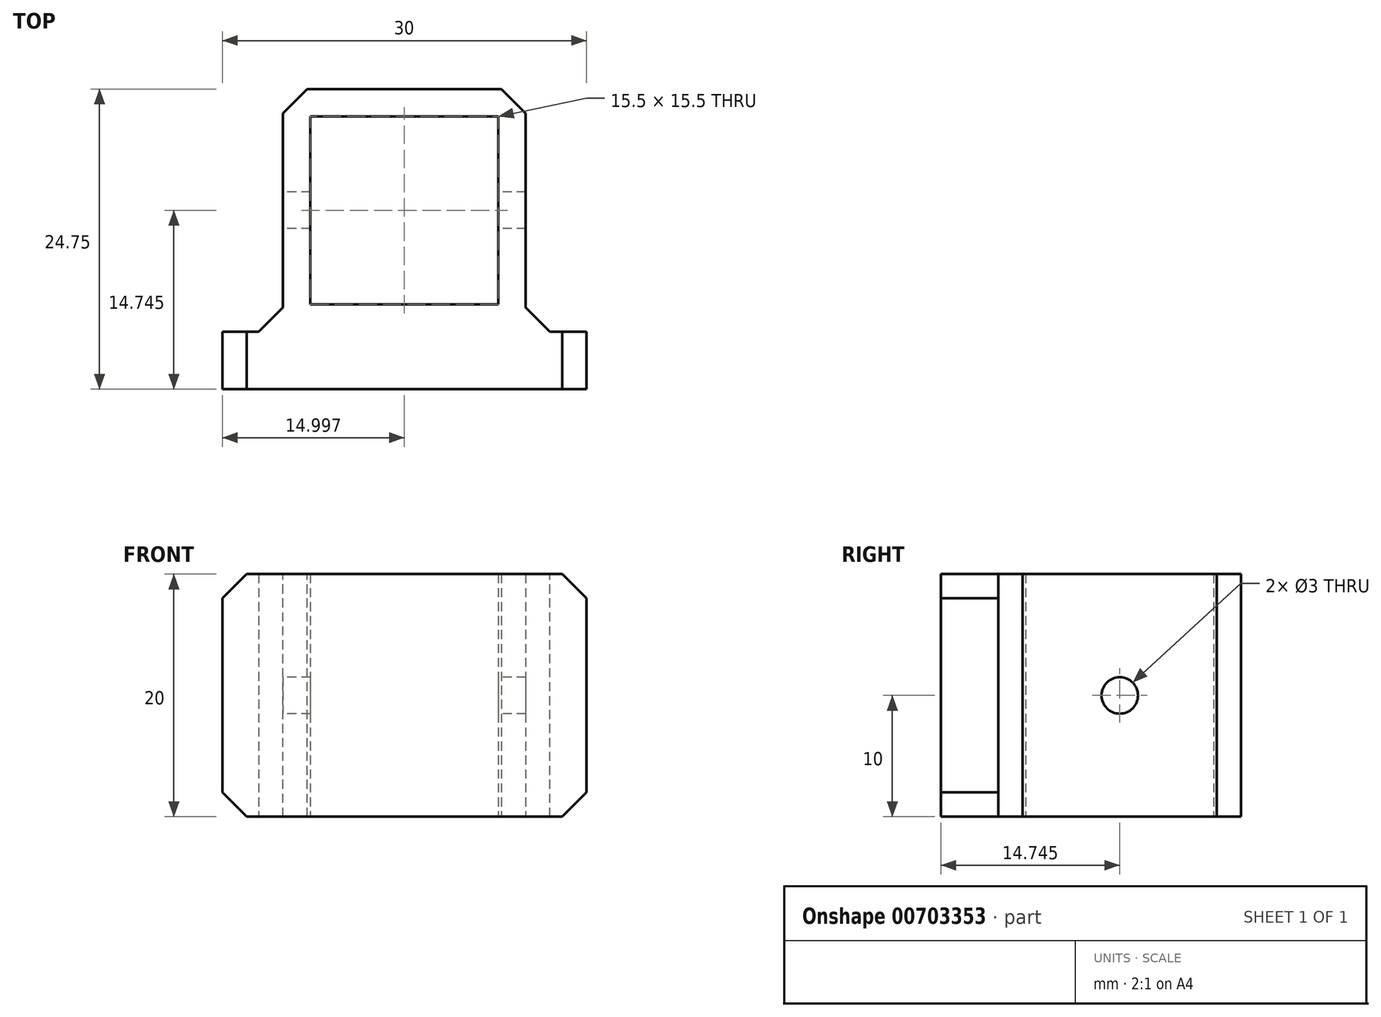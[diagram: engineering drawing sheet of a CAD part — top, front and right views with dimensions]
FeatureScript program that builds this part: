
annotation { "Feature Type Name" : "Feature", "Feature Type Description" : "" }
export const myFeature = defineFeature(function(context is Context, id is Id, definition is map)
    precondition{}
    {
        {
            var Q0;
            Q0=qCreatedBy(makeId("Top.planeOp"),FACE);
            var sketch = newSketch(context, id + "F0", { "sketchPlane" : qUnion([Q0])});
            skLineSegment(sketch, "E0.bottom", {"start": v(-33.17, 14.56) * mm, "end": v(-48.67, 14.56) * mm});
            skLineSegment(sketch, "E0.top", {"start": v(-33.17, 30.06) * mm, "end": v(-48.67, 30.06) * mm});
            skLineSegment(sketch, "E0.left", {"start": v(-33.17, 14.56) * mm, "end": v(-33.17, 30.06) * mm});
            skLineSegment(sketch, "E0.right", {"start": v(-48.67, 14.56) * mm, "end": v(-48.67, 30.06) * mm});
            skPoint(sketch, "E0.middle", {"position": v(-40.92, 22.3) * mm});
            skLineSegment(sketch, "E1.bottom", {"start": v(-50.92, 12.3) * mm, "end": v(-30.92, 12.3) * mm});
            skLineSegment(sketch, "E1.top", {"start": v(-50.92, 32.3) * mm, "end": v(-30.92, 32.3) * mm});
            skLineSegment(sketch, "E1.left", {"start": v(-50.92, 12.3) * mm, "end": v(-50.92, 32.3) * mm});
            skLineSegment(sketch, "E1.right", {"start": v(-30.92, 12.3) * mm, "end": v(-30.92, 32.3) * mm});
            skLineSegment(sketch, "E2", {"start": v(-50.92, 12.3) * mm, "end": v(-55.92, 12.3) * mm});
            skLineSegment(sketch, "E3", {"start": v(-55.92, 12.3) * mm, "end": v(-55.92, 7.56) * mm});
            skLineSegment(sketch, "E4", {"start": v(-55.92, 7.56) * mm, "end": v(-25.92, 7.56) * mm});
            skLineSegment(sketch, "E5", {"start": v(-30.92, 12.3) * mm, "end": v(-25.92, 12.3) * mm});
            skLineSegment(sketch, "E6", {"start": v(-25.92, 12.3) * mm, "end": v(-25.92, 7.56) * mm});
            skLineSegment(sketch, "E7", {"start": v(-13.17, 18.53) * mm, "end": v(-13.17, -6.15) * mm, "construction": true});
            skSolve(sketch);
        }
        {
            var Q0;
            Q0=makeQuery(id+"F0.imprint","IMPRINT",FACE,{"disambiguationData":[TD([[makeQuery(id+"F0.imprint","IMPRINT",EDGE,{"derivedFrom":sQuery(id+"F0.wireOp",EDGE,"E0.bottom")}),1.0]])]});
            var Q1;
            Q1=makeQuery(id+"F0.imprint","IMPRINT",FACE,{"disambiguationData":[TD([[makeQuery(id+"F0.imprint","IMPRINT",EDGE,{"derivedFrom":sQuery(id+"F0.wireOp",EDGE,"E1.bottom")}),-1.0]])]});
            extrude(context, id + "F1", {"entities" : qUnion([Q0, Q1]), "depth" : 20 * mm, "offsetDistance" : 25 * mm});
        }
        {
            var Q0;
            Q0=makeQuery(id+"F1.opExtrude","SWEPT_EDGE",EDGE,{"disambiguationData":[OSD([sQuery(id+"F0.wireOp",EDGE,"E1.top"),sQuery(id+"F0.wireOp",EDGE,"E1.left")])]});
            var Q1;
            Q1=makeQuery(id+"F1.opExtrude","SWEPT_EDGE",EDGE,{"disambiguationData":[OSD([sQuery(id+"F0.wireOp",EDGE,"E1.top"),sQuery(id+"F0.wireOp",EDGE,"E1.right")])]});
            var Q2;
            Q2=makeQuery(id+"F1.opExtrude","CAP_EDGE",EDGE,{"disambiguationData":[OSD([sQuery(id+"F0.wireOp",EDGE,"E6")])],"isStart":false});
            var Q3;
            Q3=makeQuery(id+"F1.opExtrude","CAP_EDGE",EDGE,{"disambiguationData":[OSD([sQuery(id+"F0.wireOp",EDGE,"E3")])],"isStart":false});
            var Q4;
            Q4=makeQuery(id+"F1.opExtrude","CAP_EDGE",EDGE,{"disambiguationData":[OSD([sQuery(id+"F0.wireOp",EDGE,"E3")])],"isStart":true});
            var Q5;
            Q5=makeQuery(id+"F1.opExtrude","CAP_EDGE",EDGE,{"disambiguationData":[OSD([sQuery(id+"F0.wireOp",EDGE,"E6")])],"isStart":true});
            var Q6;
            Q6=makeQuery(id+"F1.opExtrude","SWEPT_EDGE",EDGE,{"disambiguationData":[OSD([sQuery(id+"F0.wireOp",EDGE,"E1.bottom"),sQuery(id+"F0.wireOp",EDGE,"E1.right"),sQuery(id+"F0.wireOp",EDGE,"E5")])]});
            var Q7;
            Q7=makeQuery(id+"F1.opExtrude","SWEPT_EDGE",EDGE,{"disambiguationData":[OSD([sQuery(id+"F0.wireOp",EDGE,"E1.bottom"),sQuery(id+"F0.wireOp",EDGE,"E1.left"),sQuery(id+"F0.wireOp",EDGE,"E2")])]});
            chamfer(context, id + "F2", {"entities" : qUnion([Q0, Q1, Q2, Q3, Q4, Q5, Q6, Q7]), "width" : 2 * mm, "tangentPropagation" : true});
        }
        {
            var Q0;
            Q0=makeQuery(id+"F1.opExtrude","SWEPT_FACE",FACE,{"disambiguationData":[OSD([sQuery(id+"F0.wireOp",EDGE,"E1.left")])]});
            var sketch = newSketch(context, id + "F3", { "sketchPlane" : qUnion([Q0])});
            skLineSegment(sketch, "E8", {"start": v(-30.3, 20) * mm, "end": v(-14.3, 0) * mm, "construction": true});
            skLineSegment(sketch, "E9", {"start": v(-14.3, 0) * mm, "end": v(-14.3, 20) * mm, "construction": true});
            skLineSegment(sketch, "E10", {"start": v(-14.3, 20) * mm, "end": v(-30.3, 0) * mm, "construction": true});
            skCircle(sketch, "E11", {"center": v(-22.3, 10) * mm, "radius": 1.5 * mm});
            skSolve(sketch);
        }
        {
            var Q0;
            Q0=makeQuery(id+"F3.imprint","IMPRINT",FACE,{"disambiguationData":[TD([[makeQuery(id+"F3.imprint","IMPRINT",EDGE,{"derivedFrom":sQuery(id+"F3.wireOp",EDGE,"E11")}),1.0]])]});
            extrude(context, id + "F4", {"entities" : qUnion([Q0]), "operationType" : NewBodyOperationType.REMOVE, "oppositeDirection" : true, "depth" : 25 * mm, "offsetDistance" : 25 * mm});
        }
    });
